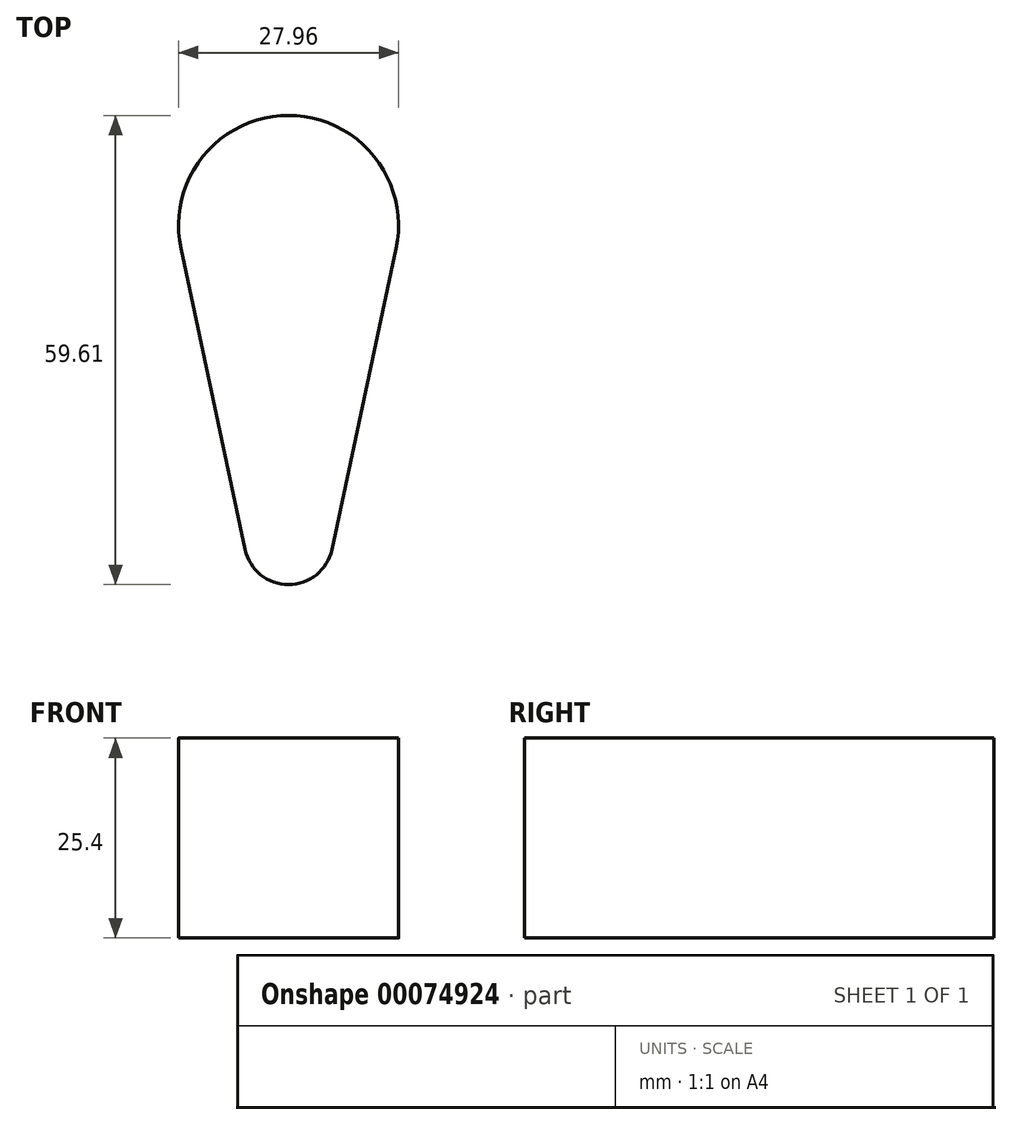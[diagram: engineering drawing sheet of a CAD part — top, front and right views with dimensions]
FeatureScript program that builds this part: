
annotation { "Feature Type Name" : "Feature", "Feature Type Description" : "" }
export const myFeature = defineFeature(function(context is Context, id is Id, definition is map)
    precondition{}
    {
        {
            var Q0;
            Q0=qCreatedBy(makeId("Top.planeOp"),FACE);
            var sketch = newSketch(context, id + "F0", { "sketchPlane" : qUnion([Q0])});
            skLineSegment(sketch, "E0", {"start": v(13.67, 0) * mm, "end": v(5.5, -38.26) * mm});
            skArc(sketch, "E1", {"start": v(5.5, -38.26) * mm, "mid": v(0, -42.71) * mm, "end": v(-5.5, -38.26) * mm});
            skLineSegment(sketch, "E2", {"start": v(-5.5, -38.26) * mm, "end": v(-13.67, 0) * mm});
            skArc(sketch, "E3", {"start": v(-13.67, 0) * mm, "mid": v(0, 16.9) * mm, "end": v(13.67, 0) * mm});
            skSolve(sketch);
        }
        {
            var Q0;
            Q0=makeQuery(id+"F0.imprint","IMPRINT",FACE,{"disambiguationData":[TD([[makeQuery(id+"F0.imprint","IMPRINT",EDGE,{"derivedFrom":sQuery(id+"F0.wireOp",EDGE,"E0")}),-1.0]])]});
            extrude(context, id + "F1", {"entities" : qUnion([Q0]), "endBound" : BoundingType.SYMMETRIC, "depth" : 25.4 * mm});
        }
    });
